# Revit family: QF_MACOM_CZ71C-2T_3T
name_source: partatom
category: Equipamento especial
units: mm (PartAtom-declared; Revit-internal decimal feet)

## family parameters
Com base no plano de trabalho = Não
Compartilhado = Não
Corte com vazios quando carregada = Não
Cota do conector redondo = Utilizar diâmetro
Número OmniClass = 23.40.40.14.17.11
Ponto de cálculo do ambiente = Não
Sempre na vertical = Sim
Tipo de parte = Normal
Título OmniClass = Cookers, Ovens, Stoves

## types (2) — shared parameters
Capacity in Liters = 18,0 L
Capacity in Liters Larger Basket = 12,0 L
Capacity in Liters Smaller Basket = 1,5 L
Cycle = 60 Hz
Degree of Protection = IP 22
Depth = 745,000 mm
Descrição = COZEDOR DE MASSAS 700HP MACOM 360 ELETRICO
Elec Connection Height = 73,000 mm
Electric Power = 9000 W
Elevação padrão = 0,000 mm
Fabricante = MACOM
Height = 1200,000 mm
Larger Basket = Sim
Operational Current = 0 A
Phase = 3
Show Clearances = Sim
Smaller Basket = Sim
URL = https://www.acosmacom.com.br
Volume = 0,33 m³
Weight = 23,00 kg
Width = 360,000 mm
Work Temperature = 50 ºC - 85ºC

## per-type parameters (varying)
| type | Volts |
| CZ71C-2T | 220 V |
| CZ71C-3T | 380 V |

note: column(s) folded — value = type name in every type: Modelo

## geometry (parser evidence)
native form markers: Sweep x19
no freeform markers — native parametric forms only
